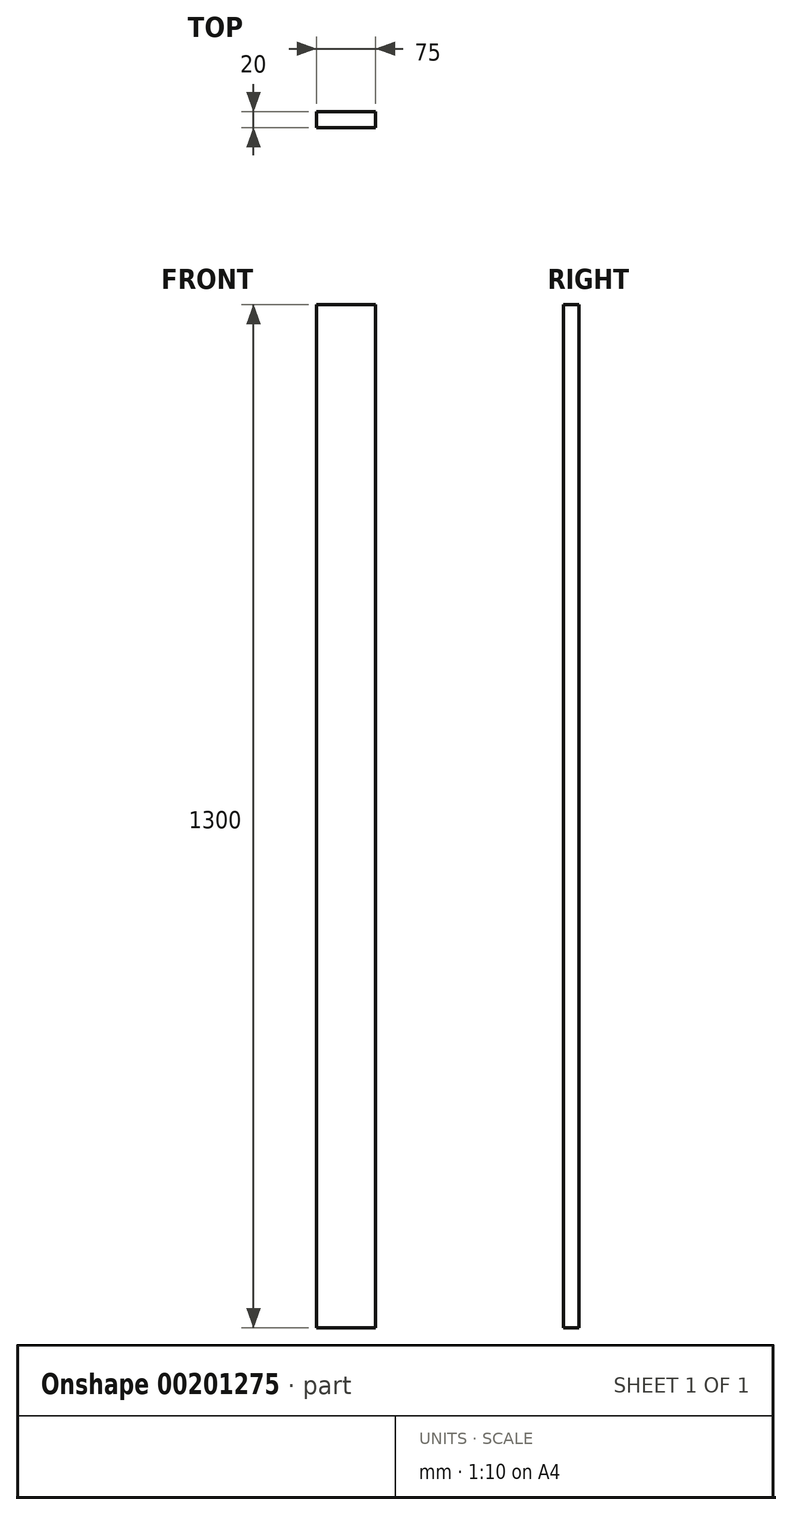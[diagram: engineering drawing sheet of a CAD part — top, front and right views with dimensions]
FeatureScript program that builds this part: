
annotation { "Feature Type Name" : "Feature", "Feature Type Description" : "" }
export const myFeature = defineFeature(function(context is Context, id is Id, definition is map)
    precondition{}
    {
        {
            var Q0;
            Q0=qCreatedBy(makeId("Top.planeOp"),FACE);
            var sketch = newSketch(context, id + "F0", { "sketchPlane" : qUnion([Q0])});
            skLineSegment(sketch, "E0.bottom", {"start": v(0, 0) * mm, "end": v(75, 0) * mm});
            skLineSegment(sketch, "E0.top", {"start": v(0, 20) * mm, "end": v(75, 20) * mm});
            skLineSegment(sketch, "E0.left", {"start": v(0, 0) * mm, "end": v(0, 20) * mm});
            skLineSegment(sketch, "E0.right", {"start": v(75, 0) * mm, "end": v(75, 20) * mm});
            skSolve(sketch);
        }
        {
            var Q0;
            Q0=qSketchRegion(id+"F0",true);
            extrude(context, id + "F1", {"entities" : qUnion([Q0]), "depth" : 1300 * mm});
        }
    });
